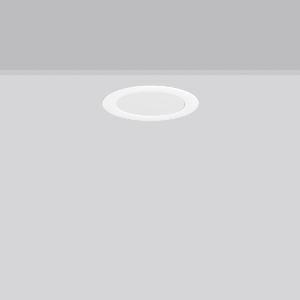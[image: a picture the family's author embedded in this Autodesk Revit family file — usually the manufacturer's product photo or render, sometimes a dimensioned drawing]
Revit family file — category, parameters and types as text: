
# Revit family: toledo_flat_round_e_672229_002_1_2804
name_source: partatom
category: Lighting Fixtures
units: mm (PartAtom-declared; Revit-internal decimal feet)

## family parameters
Cut with Voids When Loaded = No
Host = Face
Light Source = No
Part Type = Normal
Room Calculation Point = No
Round Connector Dimension = Use Diameter
Shared = No

## types (1)
- TOLEDO FLAT round E (1 x LED Modul 840, 840 lm, 4000)
    Apparent Load = 8 VA
    CIE Flux Codes = 47 79 96 100 100
    Color Rendering = 80
    Color Temperature = 4000
    Default Elevation = 1800 mm
    Description = Series: TOLEDO FLAT round
Ultra thin recessed downlight. For escape route illumination. Housing: die-cast aluminium, powder-coated. Lightguide and diffuser made of non-yellowing plastic (PMMA). Diffuser opal matt plastic. Ceiling installation with spring system. Including separate LED converter with connecting cable 250 mm. Suitable for connection to central battery systems. External driver with simple plug-in locking system. 
Colour: white
Diameter: 190 mm
Height: 2.5 mm
Cut-out diameter: 170 mm
Recess height: 35 mm
Luminaire: recess height: 31-51 mm
Weight: 413 g
Operating mode: maintained power mode
Lamp: LED
Socket: without socket
Colour temperature: 4000K
Colour rendering index (CRI): 80
System power: 7.7 W
Rated luminous flux: 840 lm
Luminous flux, emergency: 840 lm
System power, emergency: 7.7 W
Control gear: Regulated power supply
Protection class: II
Type of protection: IP 54
    Height = 0 mm  [stored 0 ft]
    Lamp = 1 x LED Modul 840
    Lamp Light Flux = 840 lm
    Lamp count = 1
    Length = 190 mm  [stored 0.62336 ft]
    Lifetime = 50000 h
    Luminous efficacy = 109 lm/W
    Manufacturer = RZB
    ModVariant = No
    Model = 672229.002.1
    Mounting Place = Ceiling
    Mounting Type = Recessed
    Number of Poles = 1
    OnlyDefault = Yes
    Power Factor = 1
    Product Name = TOLEDO FLAT round E
    Product group = Recessed downlights
    ProductGroupID = 402
    Protection Class = Protection class II
    Protection Degree = IP 40
    RLX_Detail_Level = 1
    RLX_Emergency_Light_Flux = 840 lm
    RLX_Emergency_Type = 3
    RLX_Emergency_Type_DB = Yes
    RlxData = <blob elided: 28857 chars, md5=9900c23b>
    Socket = socket
    Standby Power = 0 W
    System Light Flux = 840 lm
    System Power = 8 W
    Type Comments = Product without accessories
    Type Image = 901452.002.jpg
    URL = http://relux.com
    VarID = ---
    Voltage = 230 V
    Voltage Range = 220-240 V
    Weight = 0.00 kg
    Width = 0 mm  [stored 0 ft]

note: [stored X ft] marks values corroborated as IEEE doubles in the binary element streams (Revit-internal decimal feet)

## geometry (parser evidence)
native form markers: Blend x4, Sweep x11
no freeform markers — native parametric forms only
